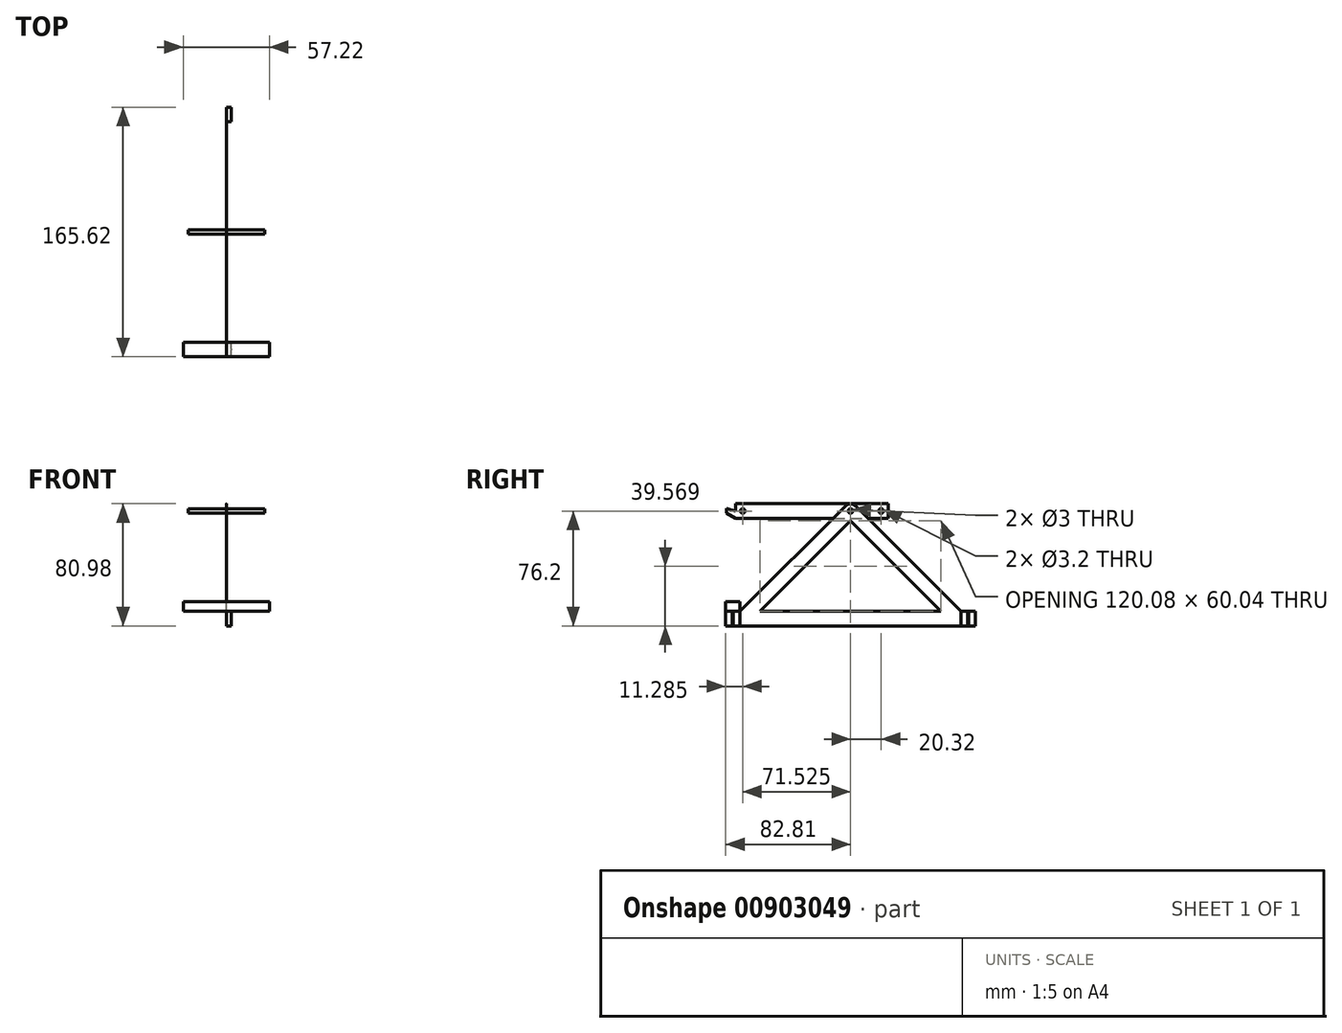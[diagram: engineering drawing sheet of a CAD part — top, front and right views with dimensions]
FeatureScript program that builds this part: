
annotation { "Feature Type Name" : "Feature", "Feature Type Description" : "" }
export const myFeature = defineFeature(function(context is Context, id is Id, definition is map)
    precondition{}
    {
        {
            assignVariable(context, id + "F0", {"name" : "minThickness", "anyValue" : 1 / 203.2 * mm});
        }
        {
            assignVariable(context, id + "F1", {"name" : "fastenerFreeSize", "anyValue" : 3.2 * mm});
        }
        {
            assignVariable(context, id + "F2", {"name" : "strutThickness", "anyValue" : 1 / 101.6 * mm});
        }
        {
            assignVariable(context, id + "F3", {"name" : "strutWidth", "anyValue" : getVariable(context, 'fastenerFreeSize') + 2 * getVariable(context, 'minThickness')});
        }
        {
            assignVariable(context, id + "F4", {"name" : "span", "anyValue" : 50.8 * mm});
        }
        {
            var Q0;
            Q0=qCreatedBy(makeId("Right.planeOp"),FACE);
            var sketch = newSketch(context, id + "F5", { "sketchPlane" : qUnion([Q0])});
            skLineSegment(sketch, "E0", {"start": v(0, 0) * mm, "end": v(0, 76.2) * mm, "construction": true});
            skCircle(sketch, "E1", {"center": v(0, 76.2) * mm, "radius": 1.5 * mm});
            skLineSegment(sketch, "E2", {"start": v(0, 76.2) * mm, "end": v(0, 80.88) * mm, "construction": true});
            skLineSegment(sketch, "E3", {"start": v(-82.81, 0) * mm, "end": v(82.81, 0) * mm, "construction": true});
            skCircle(sketch, "E4", {"center": v(0, 76.2) * mm, "radius": 4.68 * mm, "construction": true});
            skLineSegment(sketch, "E5", {"start": v(-82.81, 0) * mm, "end": v(-3.3, 79.5) * mm, "construction": true});
            skLineSegment(sketch, "E6", {"start": v(82.81, 0) * mm, "end": v(3.3, 79.5) * mm, "construction": true});
            skLineSegment(sketch, "E7.bottom", {"start": v(-82.81, 0) * mm, "end": v(82.81, 0) * mm});
            skLineSegment(sketch, "E7.top", {"start": v(-82.81, 9.55) * mm, "end": v(82.81, 9.55) * mm});
            skLineSegment(sketch, "E7.left", {"start": v(-82.81, 0) * mm, "end": v(-82.81, 9.55) * mm});
            skLineSegment(sketch, "E7.right", {"start": v(82.81, 0) * mm, "end": v(82.81, 9.55) * mm});
            skLineSegment(sketch, "E8", {"start": v(-73.26, 9.55) * mm, "end": v(-3.3, 79.5) * mm});
            skLineSegment(sketch, "E9", {"start": v(73.26, 9.55) * mm, "end": v(3.3, 79.5) * mm});
            skArc(sketch, "E10", {"start": v(-3.3, 79.5) * mm, "mid": v(0, 80.87) * mm, "end": v(3.3, 79.5) * mm});
            skLineSegment(sketch, "E11", {"start": v(-60.04, 9.55) * mm, "end": v(0, 69.59) * mm});
            skLineSegment(sketch, "E12", {"start": v(0, 69.59) * mm, "end": v(60.04, 9.55) * mm});
            skLineSegment(sketch, "E13.bottom", {"start": v(-73.26, 9.55) * mm, "end": v(-82.81, 9.55) * mm});
            skLineSegment(sketch, "E13.top", {"start": v(-73.26, 15.9) * mm, "end": v(-82.81, 15.9) * mm});
            skLineSegment(sketch, "E13.left", {"start": v(-73.26, 9.55) * mm, "end": v(-73.26, 15.9) * mm});
            skLineSegment(sketch, "E13.right", {"start": v(-82.81, 9.55) * mm, "end": v(-82.81, 15.9) * mm});
            skLineSegment(sketch, "E14.bottom", {"start": v(73.26, 9.55) * mm, "end": v(82.81, 9.55) * mm});
            skLineSegment(sketch, "E14.top", {"start": v(73.26, 15.9) * mm, "end": v(82.81, 15.9) * mm});
            skLineSegment(sketch, "E14.left", {"start": v(73.26, 9.55) * mm, "end": v(73.26, 15.9) * mm});
            skLineSegment(sketch, "E14.right", {"start": v(82.81, 9.55) * mm, "end": v(82.81, 15.9) * mm});
            skLineSegment(sketch, "E15", {"start": v(-73.26, 9.55) * mm, "end": v(-73.26, 0) * mm});
            skLineSegment(sketch, "E16", {"start": v(73.26, 9.55) * mm, "end": v(73.26, 0) * mm});
            skSolve(sketch);
        }
        {
            var Q0;
            Q0=qCreatedBy(makeId("Right.planeOp"),FACE);
            var sketch = newSketch(context, id + "F6", { "sketchPlane" : qUnion([Q0])});
            skPoint(sketch, "E17.0", {"position": v(0, 76.2) * mm});
            skCircle(sketch, "E18", {"center": v(0, 76.2) * mm, "radius": 1.6 * mm});
            skLineSegment(sketch, "E19.bottom", {"start": v(-76.2, 80.97) * mm, "end": v(25.1, 80.97) * mm});
            skLineSegment(sketch, "E19.top", {"start": v(-76.2, 71.42) * mm, "end": v(25.1, 71.42) * mm});
            skLineSegment(sketch, "E19.left", {"start": v(-76.2, 80.97) * mm, "end": v(-76.2, 71.42) * mm});
            skLineSegment(sketch, "E19.right", {"start": v(25.1, 80.97) * mm, "end": v(25.1, 71.42) * mm});
            skLineSegment(sketch, "E20", {"start": v(0, 80.97) * mm, "end": v(0, 71.42) * mm, "construction": true});
            skCircle(sketch, "E21", {"center": v(20.32, 76.2) * mm, "radius": 1.6 * mm});
            skLineSegment(sketch, "E22", {"start": v(-76.2, 76.2) * mm, "end": v(-82.33, 77.84) * mm});
            skLineSegment(sketch, "E23", {"start": v(-82.33, 77.84) * mm, "end": v(-82.33, 74.67) * mm});
            skLineSegment(sketch, "E24", {"start": v(-82.33, 74.67) * mm, "end": v(-76.2, 71.42) * mm});
            skCircle(sketch, "E25", {"center": v(-71.53, 76.2) * mm, "radius": 1.5 * mm});
            skLineSegment(sketch, "E26", {"start": v(-76.2, 76.2) * mm, "end": v(-93.94, 76.2) * mm, "construction": true});
            skSolve(sketch);
        }
        {
            var Q0;
            {var subQ2=sQuery(id+"F5.wireOp",EDGE,"E7.left");Q0=makeQuery(id+"F5.imprint","IMPRINT",FACE,{"disambiguationData":[TD([[makeQuery(id+"F5.imprint","IMPRINT",EDGE,{"derivedFrom":subQ2}),-1.0]])]});}
            var Q1;
            {var subQ0=sQuery(id+"F5.wireOp",EDGE,"E7.right");Q1=makeQuery(id+"F5.imprint","IMPRINT",FACE,{"disambiguationData":[TD([[makeQuery(id+"F5.imprint","IMPRINT",EDGE,{"derivedFrom":subQ0}),1.0]])]});}
            extrude(context, id + "F7", {"entities" : qUnion([Q0, Q1]), "depth" : getVariable(context, 'strutWidth'), "offsetDistance" : 25.4 * mm});
        }
        {
            var Q0;
            Q0=makeQuery(id+"F5.imprint","IMPRINT",FACE,{"disambiguationData":[TD([[makeQuery(id+"F5.imprint","IMPRINT",EDGE,{"derivedFrom":sQuery(id+"F5.wireOp",EDGE,"E1")}),-1.0]])]});
            var Q1;
            {var subQ4=sQuery(id+"F5.wireOp",EDGE,"E15");Q1=makeQuery(id+"F5.imprint","IMPRINT",FACE,{"disambiguationData":[TD([[makeQuery(id+"F5.imprint","IMPRINT",EDGE,{"derivedFrom":subQ4}),1.0]])]});}
            extrude(context, id + "F8", {"entities" : qUnion([Q0, Q1]), "operationType" : NewBodyOperationType.ADD, "depth" : getVariable(context, 'strutThickness'), "offsetDistance" : 25.4 * mm});
        }
        {
            var Q0;
            Q0=makeQuery(id+"F5.imprint","IMPRINT",FACE,{"disambiguationData":[TD([[makeQuery(id+"F5.imprint","IMPRINT",EDGE,{"derivedFrom":sQuery(id+"F5.wireOp",EDGE,"E13.top")}),1.0]])]});
            extrude(context, id + "F9", {"entities" : qUnion([Q0]), "endBound" : BoundingType.SYMMETRIC, "depth" : getVariable(context, 'span') + getVariable(context, 'strutWidth') * 2, "offsetDistance" : 25.4 * mm});
        }
        {
            var Q0;
            Q0=makeQuery(id+"F9.opExtrude","SWEPT_FACE",FACE,{"disambiguationData":[OSD([sQuery(id+"F5.wireOp",EDGE,"E13.top")])]});
            var sketch = newSketch(context, id + "F10", { "sketchPlane" : qUnion([Q0])});
            skLineSegment(sketch, "E27", {"start": v(34.95, -82.81) * mm, "end": v(25.4, -73.26) * mm, "construction": true});
            skLineSegment(sketch, "E28", {"start": v(-34.95, -82.81) * mm, "end": v(-25.4, -73.26) * mm, "construction": true});
            skCircle(sketch, "E29", {"center": v(-30.18, -78.04) * mm, "radius": 1.5 * mm});
            skCircle(sketch, "E30", {"center": v(30.18, -78.04) * mm, "radius": 1.5 * mm});
            skSolve(sketch);
        }
        {
            var Q0;
            Q0=makeQuery(id+"F10.imprint","IMPRINT",FACE,{"disambiguationData":[TD([[makeQuery(id+"F10.imprint","IMPRINT",EDGE,{"derivedFrom":sQuery(id+"F10.wireOp",EDGE,"E30")}),1.0]])]});
            var Q1;
            Q1=makeQuery(id+"F10.imprint","IMPRINT",FACE,{"disambiguationData":[TD([[makeQuery(id+"F10.imprint","IMPRINT",EDGE,{"derivedFrom":sQuery(id+"F10.wireOp",EDGE,"E29")}),1.0]])]});
            var Q2;
            Q2=makeQuery(id+"F9.opExtrude","SWEPT_FACE",FACE,{"disambiguationData":[OSD([sQuery(id+"F5.wireOp",EDGE,"E7.top")])]});
            extrude(context, id + "F11", {"entities" : qUnion([Q0, Q1]), "operationType" : NewBodyOperationType.REMOVE, "endBound" : BoundingType.UP_TO_SURFACE, "oppositeDirection" : true, "depth" : 25.4 * mm, "endBoundEntityFace" : qUnion([Q2]), "offsetDistance" : 25.4 * mm});
        }
        {
            var Q0;
            {var subQ0=sQuery(id+"F5.wireOp",EDGE,"E7.bottom");Q0=makeQuery(id+"F8.boolean.opBoolean","MERGE",FACE,{"derivedFrom":[makeQuery(id+"F7.opExtrude","SWEPT_FACE",FACE,{"disambiguationData":[OSD([subQ0]),TDD([makeQuery(id+"F5.imprint","IMPRINT",EDGE,{"disambiguationData":[TD([[makeQuery(id+"F5.imprint","INTERSECT",VERTEX,{"derivedFrom":[subQ0,sQuery(id+"F5.wireOp",EDGE,"E15")]}),1.0]])],"derivedFrom":subQ0})])]}),makeQuery(id+"F7.opExtrude","SWEPT_FACE",FACE,{"disambiguationData":[OSD([subQ0]),TDD([makeQuery(id+"F5.imprint","IMPRINT",EDGE,{"disambiguationData":[TD([[makeQuery(id+"F5.imprint","INTERSECT",VERTEX,{"derivedFrom":[subQ0,sQuery(id+"F5.wireOp",EDGE,"E7.right")]}),1.0]])],"derivedFrom":subQ0})])]}),makeQuery(id+"F8.opExtrude","SWEPT_FACE",FACE,{"disambiguationData":[OSD([subQ0])]})]});}
            var sketch = newSketch(context, id + "F12", { "sketchPlane" : qUnion([Q0])});
            skLineSegment(sketch, "E31", {"start": v(9.55, 73.26) * mm, "end": v(0, 82.81) * mm, "construction": true});
            skLineSegment(sketch, "E32", {"start": v(9.55, -73.26) * mm, "end": v(0, -82.81) * mm, "construction": true});
            skCircle(sketch, "E33", {"center": v(4.77, -78.04) * mm, "radius": 1.6 * mm});
            skCircle(sketch, "E34", {"center": v(4.77, 78.04) * mm, "radius": 1.6 * mm});
            skSolve(sketch);
        }
        {
            var Q0;
            Q0=makeQuery(id+"F12.imprint","IMPRINT",FACE,{"disambiguationData":[TD([[makeQuery(id+"F12.imprint","IMPRINT",EDGE,{"derivedFrom":sQuery(id+"F12.wireOp",EDGE,"E34")}),1.0]])]});
            var Q1;
            Q1=makeQuery(id+"F12.imprint","IMPRINT",FACE,{"disambiguationData":[TD([[makeQuery(id+"F12.imprint","IMPRINT",EDGE,{"derivedFrom":sQuery(id+"F12.wireOp",EDGE,"E33")}),1.0]])]});
            var Q2;
            {var subQ0=sQuery(id+"F5.wireOp",EDGE,"E7.top");Q2=makeQuery(id+"F7.opExtrude","SWEPT_FACE",FACE,{"disambiguationData":[OSD([subQ0]),TDD([makeQuery(id+"F5.imprint","IMPRINT",EDGE,{"disambiguationData":[TD([[makeQuery(id+"F5.imprint","INTERSECT",VERTEX,{"derivedFrom":[subQ0,sQuery(id+"F5.wireOp",EDGE,"E7.left"),sQuery(id+"F5.wireOp",EDGE,"E13.right")]}),-1.0]])],"derivedFrom":subQ0})])]});}
            extrude(context, id + "F13", {"entities" : qUnion([Q0, Q1]), "operationType" : NewBodyOperationType.REMOVE, "endBound" : BoundingType.UP_TO_SURFACE, "oppositeDirection" : true, "depth" : 25.4 * mm, "endBoundEntityFace" : qUnion([Q2]), "offsetDistance" : 25.4 * mm});
        }
        {
            var Q0;
            Q0=makeQuery(id+"F6.imprint","IMPRINT",FACE,{"disambiguationData":[TD([[makeQuery(id+"F6.imprint","IMPRINT",EDGE,{"derivedFrom":sQuery(id+"F6.wireOp",EDGE,"E18")}),-1.0]])]});
            var Q1;
            {var subQ2=sQuery(id+"F6.wireOp",EDGE,"E22");Q1=makeQuery(id+"F6.imprint","IMPRINT",FACE,{"disambiguationData":[TD([[makeQuery(id+"F6.imprint","IMPRINT",EDGE,{"derivedFrom":subQ2}),1.0]])]});}
            extrude(context, id + "F14", {"entities" : qUnion([Q0, Q1]), "endBound" : BoundingType.SYMMETRIC, "depth" : getVariable(context, 'strutThickness'), "offsetDistance" : 25.4 * mm});
        }
        {
            var Q0;
            Q0=makeQuery(id+"F5.imprint","IMPRINT",FACE,{"disambiguationData":[TD([[makeQuery(id+"F5.imprint","IMPRINT",EDGE,{"derivedFrom":sQuery(id+"F5.wireOp",EDGE,"E1")}),1.0]])]});
            extrude(context, id + "F15", {"entities" : qUnion([Q0]), "endBound" : BoundingType.SYMMETRIC, "depth" : getVariable(context, 'span') + 4 * getVariable(context, 'strutThickness'), "offsetDistance" : 25.4 * mm});
        }
    });
